# Revit family: LRDCH
name_source: partatom
category: Lighting Fixtures
units: mm (PartAtom-declared; Revit-internal decimal feet)

## family parameters
Cut with Voids When Loaded = No
Host = Face
Light Source = Yes
Maintain Annotation Orientation = No
Part Type = Normal
Room Calculation Point = No
Round Connector Dimension = Use Diameter
Shared = No

## types (6) — shared parameters
Assembly Code = D5020200
Color Filter = 16777215
Default Elevation = 4' - 0"
Description = RECESSED T-BAR DATA CENTER LED LUMINAIRE
Dimming Lamp Color Temperature Shift = <None>
Emit Shape Visible in Rendering = No
Housing Finish = Metal - Viscor - White
Lamp = LED
Lens Finish = Acrylic - Viscor - Frosted Round
Manufacturer = VISIONEERING by VISCOR
Model = LRDCH
Tilt Angle = -90.00°
URL = https://viscor.com
Voltage = 120 V

## per-type parameters (varying)
| type | Apparent Load | Cover Width | Emit from Rectangle Length | Emit from Rectangle Width | Lamp Wattage | Length | Photometric Web File | Width |
| LRDCH1x4-LED840K040LUNV | 33 VA | 0' - 5 7/8" | 3' - 11 3/4" | 0' - 11 3/4" | 33 VA | 3' - 11 3/4" | LRDCH1x4-LED840K040LUNV.IES | 0' - 11 3/4" |
| LRDCH2X2-LED840K020LUNV | 14 VA | 0' - 11 7/8" | 1' - 11 3/4" | 1' - 11 3/4" | 14 VA | 1' - 11 3/4" | LRDCH2X2-LED840K020LUNV.ies | 1' - 11 3/4" |
| LRTH2X2-LED840K032LUNV | 23 VA | 0' - 11 7/8" | 1' - 11 3/4" | 1' - 11 3/4" | 23 VA | 1' - 11 3/4" | LRDCH2X2-LED840K032LUNV.ies | 1' - 11 3/4" |
| LRDCH2x4-LED840K100LUNV | 70 VA | 0' - 11 7/8" | 3' - 11 3/4" | 1' - 11 3/4" | 70 VA | 3' - 11 3/4" | LRDCH2X4-LED840K100LUNV.ies | 1' - 11 3/4" |
| LRDCH2x4-LED840K080LUNV | 57 VA | 0' - 11 7/8" | 3' - 11 3/4" | 1' - 11 3/4" | 57 VA | 3' - 11 3/4" | LRDCH2X4-LED840K080LUNV.ies | 1' - 11 3/4" |
| LRDCH1X4-LED840K060LUNV | 43 VA | 0' - 5 7/8" | 3' - 11 3/4" | 0' - 11 3/4" | 43 VA | 3' - 11 3/4" | LRDCH1X4-LED840K060LUNV.ies | 0' - 11 3/4" |

## geometry (parser evidence)
native form markers: Sweep x3
no freeform markers — native parametric forms only
